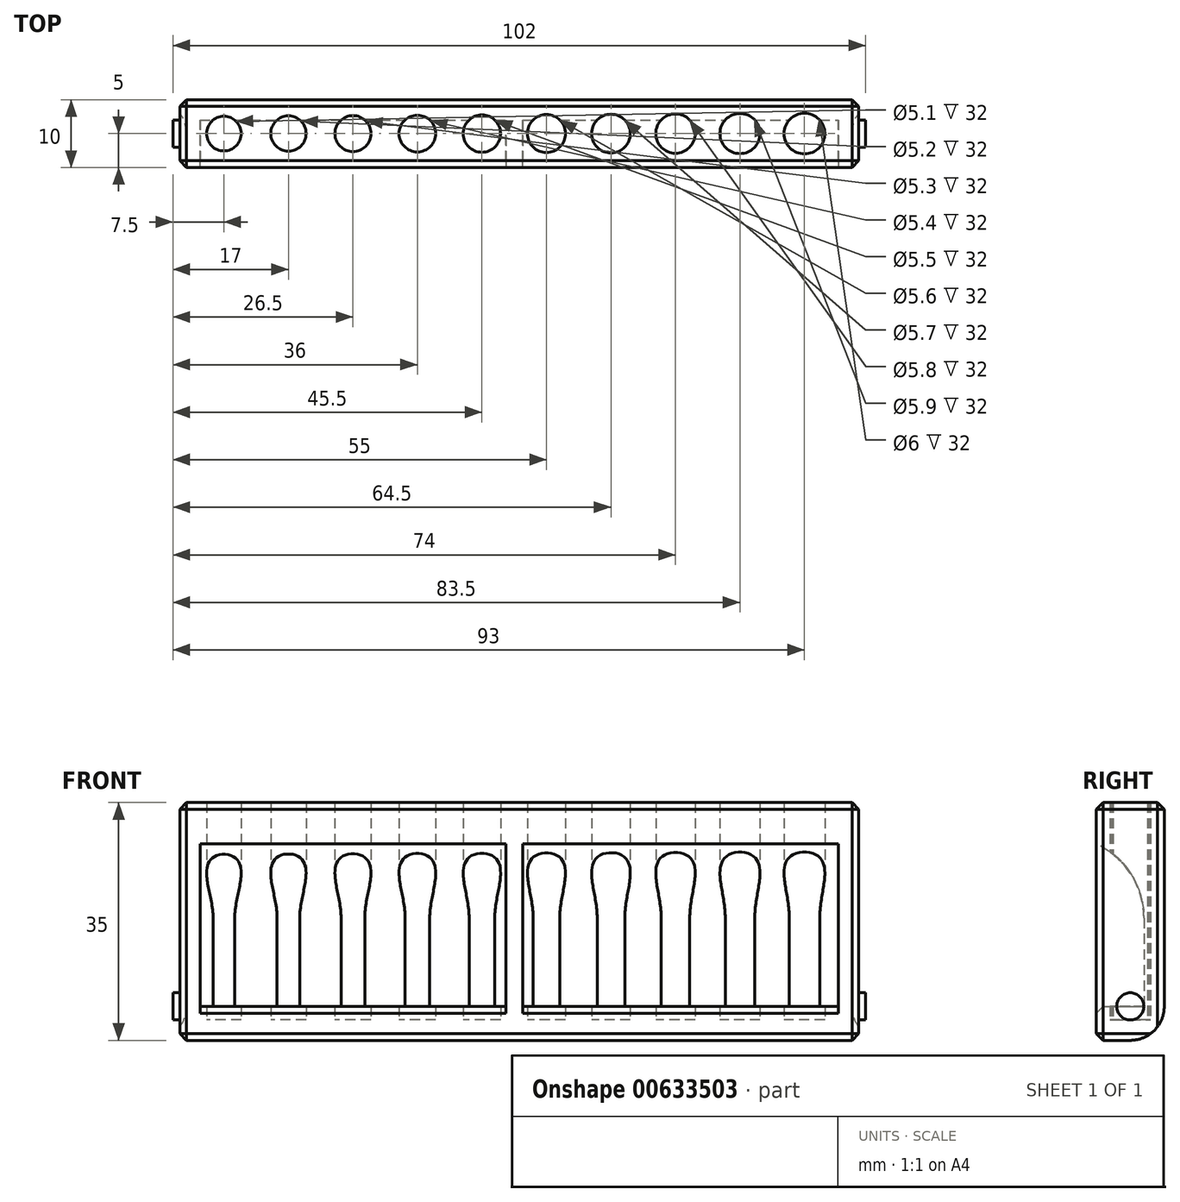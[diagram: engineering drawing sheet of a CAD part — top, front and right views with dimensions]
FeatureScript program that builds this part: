
annotation { "Feature Type Name" : "Feature", "Feature Type Description" : "" }
export const myFeature = defineFeature(function(context is Context, id is Id, definition is map)
    precondition{}
    {
        {
            var Q0;
            Q0=qCreatedBy(makeId("Top.planeOp"),FACE);
            var sketch = newSketch(context, id + "F0", { "sketchPlane" : qUnion([Q0])});
            skLineSegment(sketch, "E0.bottom", {"start": v(0, 0) * mm, "end": v(-100, 0) * mm});
            skLineSegment(sketch, "E0.top", {"start": v(0, -10) * mm, "end": v(-100, -10) * mm});
            skLineSegment(sketch, "E0.left", {"start": v(0, 0) * mm, "end": v(0, -10) * mm});
            skLineSegment(sketch, "E0.right", {"start": v(-100, 0) * mm, "end": v(-100, -10) * mm});
            skSolve(sketch);
        }
        {
            var Q0;
            Q0=qCreatedBy(makeId("Top.planeOp"),FACE);
            var sketch = newSketch(context, id + "F1", { "sketchPlane" : qUnion([Q0])});
            skLineSegment(sketch, "E1", {"start": v(0, 0) * mm, "end": v(0, -5) * mm, "construction": true});
            skLineSegment(sketch, "E2", {"start": v(0, -5) * mm, "end": v(-105.87, -5) * mm, "construction": true});
            skLineSegment(sketch, "E3", {"start": v(0, -5) * mm, "end": v(0, -25) * mm});
            skLineSegment(sketch, "E4", {"start": v(0, -25) * mm, "end": v(-8, -25) * mm});
            skLineSegment(sketch, "E5", {"start": v(-8, -25) * mm, "end": v(-8, 5) * mm, "construction": true});
            skCircle(sketch, "E6", {"center": v(-8, -5) * mm, "radius": 3 * mm});
            skCircle(sketch, "E7.1.0.0", {"center": v(-17.5, -5) * mm, "radius": 2.95 * mm});
            skCircle(sketch, "E7.2.0.0", {"center": v(-27, -5) * mm, "radius": 2.9 * mm});
            skCircle(sketch, "E7.3.0.0", {"center": v(-36.5, -5) * mm, "radius": 2.85 * mm});
            skCircle(sketch, "E7.4.0.0", {"center": v(-46, -5) * mm, "radius": 2.8 * mm});
            skCircle(sketch, "E7.5.0.0", {"center": v(-55.5, -5) * mm, "radius": 2.75 * mm});
            skCircle(sketch, "E7.6.0.0", {"center": v(-65, -5) * mm, "radius": 2.7 * mm});
            skCircle(sketch, "E7.7.0.0", {"center": v(-74.5, -5) * mm, "radius": 2.65 * mm});
            skCircle(sketch, "E7.8.0.0", {"center": v(-84, -5) * mm, "radius": 2.6 * mm});
            skCircle(sketch, "E7.9.0.0", {"center": v(-93.5, -5) * mm, "radius": 2.55 * mm});
            skLineSegment(sketch, "E7.direction1", {"start": v(-8, -5) * mm, "end": v(-17.5, -5) * mm, "construction": true});
            skSolve(sketch);
        }
        {
            var Q0;
            Q0=makeQuery(id+"F0.imprint","IMPRINT",FACE,{"disambiguationData":[TD([[makeQuery(id+"F0.imprint","IMPRINT",EDGE,{"derivedFrom":sQuery(id+"F0.wireOp",EDGE,"E0.bottom")}),1.0]])]});
            extrude(context, id + "F2", {"entities" : qUnion([Q0]), "depth" : 35 * mm, "offsetDistance" : 25 * mm});
        }
        {
            var Q0;
            Q0=qSketchRegion(id+"F1",true);
            extrude(context, id + "F3", {"entities" : qUnion([Q0]), "operationType" : NewBodyOperationType.REMOVE, "depth" : 40 * mm, "offsetDistance" : 25 * mm, "hasSecondDirection" : true, "secondDirectionOppositeDirection" : false, "secondDirectionDepth" : 3 * mm});
        }
        {
            var Q0;
            Q0=qCreatedBy(makeId("Right.planeOp"),FACE);
            var sketch = newSketch(context, id + "F4", { "sketchPlane" : qUnion([Q0])});
            skLineSegment(sketch, "E8.bottom", {"start": v(-13, 5) * mm, "end": v(-3, 5) * mm});
            skLineSegment(sketch, "E8.top", {"start": v(-15, 30) * mm, "end": v(-13, 30) * mm});
            skLineSegment(sketch, "E8.left", {"start": v(-13, 5) * mm, "end": v(-13, 30) * mm});
            skLineSegment(sketch, "E8.right", {"start": v(-3, 5) * mm, "end": v(-3, 18) * mm});
            skPoint(sketch, "E9.visualSharp", {"position": v(-3, 30) * mm});
            skArc(sketch, "E9.filletArc", {"start": v(-3, 18) * mm, "mid": v(-6.51, 26.49) * mm, "end": v(-15, 30) * mm});
            skSolve(sketch);
        }
        {
            var Q0;
            Q0=qSketchRegion(id+"F4",true);
            extrude(context, id + "F5", {"entities" : qUnion([Q0]), "operationType" : NewBodyOperationType.REMOVE, "oppositeDirection" : true, "depth" : 49.5 * mm, "offsetDistance" : 25 * mm, "hasSecondDirection" : true, "secondDirectionOppositeDirection" : true, "secondDirectionDepth" : 3 * mm});
        }
        {
            var Q0;
            Q0=qSketchRegion(id+"F4",true);
            extrude(context, id + "F6", {"entities" : qUnion([Q0]), "operationType" : NewBodyOperationType.REMOVE, "oppositeDirection" : true, "depth" : 97 * mm, "offsetDistance" : 25 * mm, "hasSecondDirection" : true, "secondDirectionOppositeDirection" : true, "secondDirectionDepth" : 52 * mm});
        }
        {
            var Q0;
            Q0=makeQuery(id+"F2.opExtrude","CAP_EDGE",EDGE,{"disambiguationData":[OSD([sQuery(id+"F0.wireOp",EDGE,"E0.top")])],"isStart":false});
            var Q1;
            Q1=makeQuery(id+"F2.opExtrude","CAP_EDGE",EDGE,{"disambiguationData":[OSD([sQuery(id+"F0.wireOp",EDGE,"E0.right")])],"isStart":false});
            var Q2;
            Q2=makeQuery(id+"F2.opExtrude","CAP_EDGE",EDGE,{"disambiguationData":[OSD([sQuery(id+"F0.wireOp",EDGE,"E0.bottom")])],"isStart":false});
            var Q3;
            Q3=makeQuery(id+"F2.opExtrude","CAP_EDGE",EDGE,{"disambiguationData":[OSD([sQuery(id+"F0.wireOp",EDGE,"E0.left")])],"isStart":false});
            var Q4;
            Q4=makeQuery(id+"F2.opExtrude","SWEPT_EDGE",EDGE,{"disambiguationData":[OSD([sQuery(id+"F0.wireOp",EDGE,"E0.top"),sQuery(id+"F0.wireOp",EDGE,"E0.left")])]});
            var Q5;
            Q5=makeQuery(id+"F2.opExtrude","SWEPT_EDGE",EDGE,{"disambiguationData":[OSD([sQuery(id+"F0.wireOp",EDGE,"E0.bottom"),sQuery(id+"F0.wireOp",EDGE,"E0.left")])]});
            var Q6;
            Q6=makeQuery(id+"F2.opExtrude","CAP_EDGE",EDGE,{"disambiguationData":[OSD([sQuery(id+"F0.wireOp",EDGE,"E0.left")])],"isStart":true});
            var Q7;
            Q7=makeQuery(id+"F2.opExtrude","CAP_EDGE",EDGE,{"disambiguationData":[OSD([sQuery(id+"F0.wireOp",EDGE,"E0.top")])],"isStart":true});
            var Q8;
            Q8=makeQuery(id+"F2.opExtrude","SWEPT_EDGE",EDGE,{"disambiguationData":[OSD([sQuery(id+"F0.wireOp",EDGE,"E0.top"),sQuery(id+"F0.wireOp",EDGE,"E0.right")])]});
            var Q9;
            Q9=makeQuery(id+"F6.boolean.opBoolean","INTERSECT",EDGE,{"derivedFrom":[makeQuery(id+"F2.opExtrude","SWEPT_FACE",FACE,{"disambiguationData":[OSD([sQuery(id+"F0.wireOp",EDGE,"E0.top")])]}),makeQuery(id+"F6.opExtrude","SWEPT_FACE",FACE,{"disambiguationData":[OSD([sQuery(id+"F4.wireOp",EDGE,"E8.bottom")])]})]});
            var Q10;
            Q10=makeQuery(id+"F5.boolean.opBoolean","INTERSECT",EDGE,{"derivedFrom":[makeQuery(id+"F2.opExtrude","SWEPT_FACE",FACE,{"disambiguationData":[OSD([sQuery(id+"F0.wireOp",EDGE,"E0.top")])]}),makeQuery(id+"F5.opExtrude","SWEPT_FACE",FACE,{"disambiguationData":[OSD([sQuery(id+"F4.wireOp",EDGE,"E8.bottom")])]})]});
            var Q11;
            Q11=makeQuery(id+"F2.opExtrude","CAP_EDGE",EDGE,{"disambiguationData":[OSD([sQuery(id+"F0.wireOp",EDGE,"E0.right")])],"isStart":true});
            var Q12;
            Q12=makeQuery(id+"F2.opExtrude","SWEPT_FACE",FACE,{"disambiguationData":[OSD([sQuery(id+"F0.wireOp",EDGE,"E0.right")])]});
            chamfer(context, id + "F7", {"entities" : qUnion([Q0, Q1, Q2, Q3, Q4, Q5, Q6, Q7, Q8, Q9, Q10, Q11, Q12]), "width" : 1 * mm, "tangentPropagation" : true});
        }
        {
            var Q0;
            Q0=qCreatedBy(makeId("Right.planeOp"),FACE);
            var sketch = newSketch(context, id + "F8", { "sketchPlane" : qUnion([Q0])});
            skLineSegment(sketch, "E10", {"start": v(0, 0) * mm, "end": v(-5, 0) * mm, "construction": true});
            skLineSegment(sketch, "E11", {"start": v(-5, 0) * mm, "end": v(-5, 5) * mm, "construction": true});
            skCircle(sketch, "E12", {"center": v(-5, 5) * mm, "radius": 2 * mm});
            skSolve(sketch);
        }
        {
            var Q0;
            Q0=makeQuery(id+"F8.imprint","IMPRINT",FACE,{"disambiguationData":[TD([[makeQuery(id+"F8.imprint","IMPRINT",EDGE,{"derivedFrom":sQuery(id+"F8.wireOp",EDGE,"E12")}),1.0]])]});
            extrude(context, id + "F9", {"entities" : qUnion([Q0]), "operationType" : NewBodyOperationType.ADD, "oppositeDirection" : true, "depth" : 2 * mm, "offsetDistance" : 25 * mm, "hasSecondDirection" : true, "secondDirectionOppositeDirection" : false, "secondDirectionDepth" : 1 * mm});
        }
        {
            var Q0;
            Q0=qSketchRegion(id+"F8",true);
            extrude(context, id + "F10", {"entities" : qUnion([Q0]), "operationType" : NewBodyOperationType.ADD, "oppositeDirection" : true, "depth" : 101 * mm, "offsetDistance" : 25 * mm, "hasSecondDirection" : true, "secondDirectionOppositeDirection" : true, "secondDirectionDepth" : 99 * mm});
        }
        {
            var Q0;
            Q0=makeQuery(id+"F2.opExtrude","CAP_EDGE",EDGE,{"disambiguationData":[OSD([sQuery(id+"F0.wireOp",EDGE,"E0.bottom")])],"isStart":true});
            fillet(context, id + "F11", {"entities" : qUnion([Q0]), "radius" : 5 * mm, "tangentPropagation" : true, "allowEdgeOverflow" : false});
        }
    });
